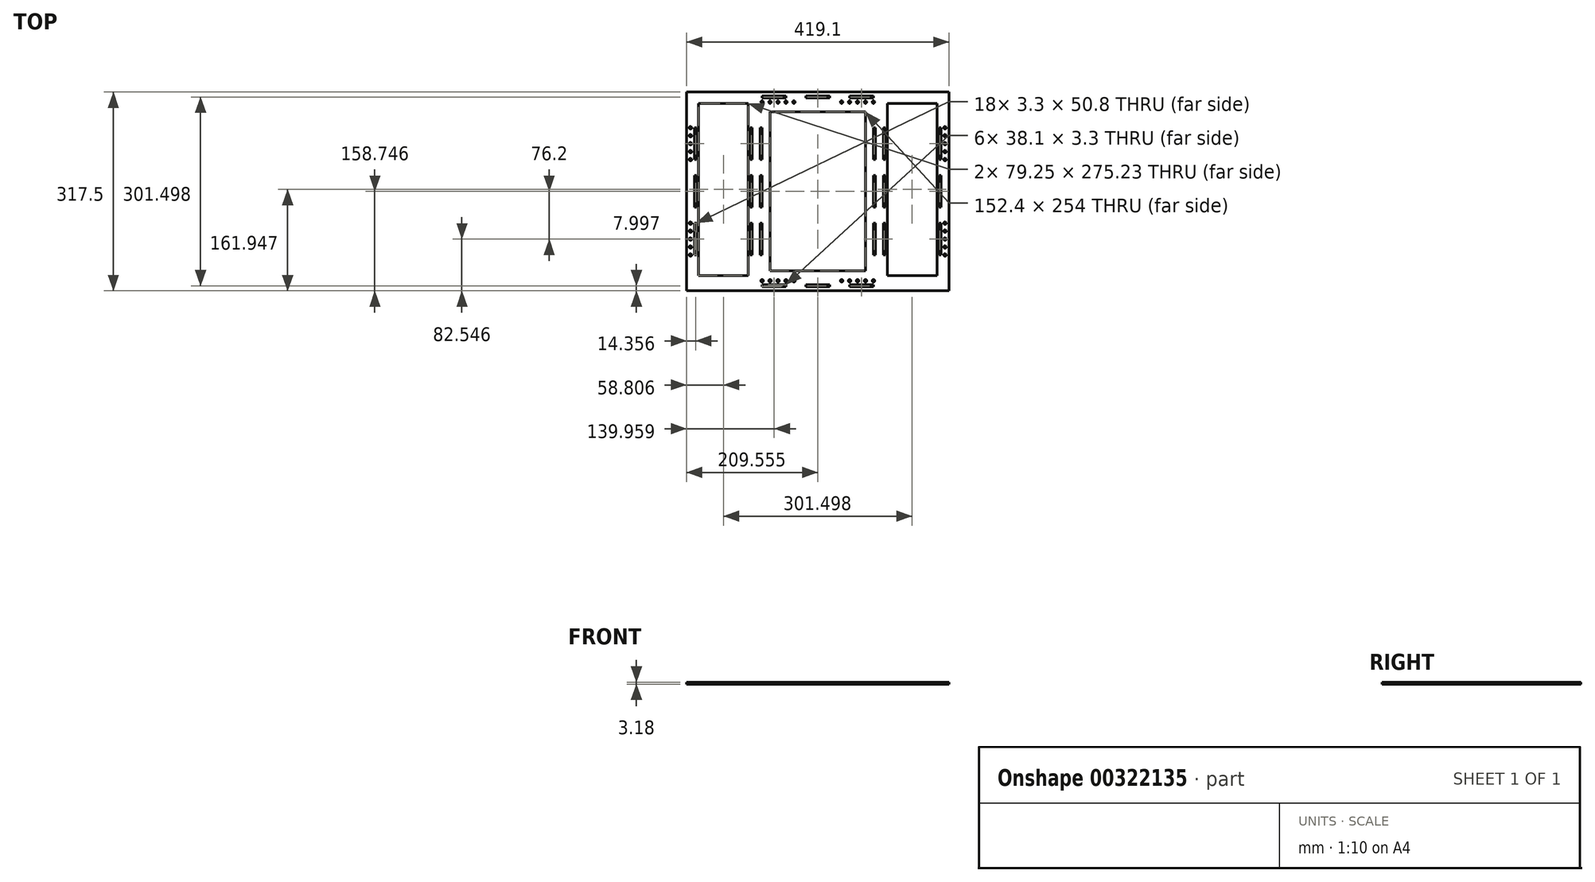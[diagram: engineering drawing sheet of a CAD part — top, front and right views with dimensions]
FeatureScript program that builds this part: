
annotation { "Feature Type Name" : "Feature", "Feature Type Description" : "" }
export const myFeature = defineFeature(function(context is Context, id is Id, definition is map)
    precondition{}
    {
        {
            var Q0;
            Q0=qCreatedBy(makeId("Top.planeOp"),FACE);
            var sketch = newSketch(context, id + "F0", { "sketchPlane" : qUnion([Q0])});
            skCircle(sketch, "E0", {"center": v(-72.78, -151.2) * mm, "radius": 1.98 * mm});
            skCircle(sketch, "E1", {"center": v(-60.08, -151.2) * mm, "radius": 1.98 * mm});
            skCircle(sketch, "E2", {"center": v(-47.38, -151.2) * mm, "radius": 1.98 * mm});
            skCircle(sketch, "E3", {"center": v(-34.68, -151.2) * mm, "radius": 1.98 * mm});
            skCircle(sketch, "E4", {"center": v(-85.48, -151.2) * mm, "radius": 1.98 * mm});
            skCircle(sketch, "E5", {"center": v(41.52, -151.2) * mm, "radius": 1.98 * mm});
            skCircle(sketch, "E6", {"center": v(54.22, -151.2) * mm, "radius": 1.98 * mm});
            skCircle(sketch, "E7", {"center": v(66.92, -151.2) * mm, "radius": 1.98 * mm});
            skCircle(sketch, "E8", {"center": v(79.62, -151.2) * mm, "radius": 1.98 * mm});
            skCircle(sketch, "E9", {"center": v(92.32, -151.2) * mm, "radius": 1.98 * mm});
            skCircle(sketch, "E10.MirrorC", {"center": v(-47.38, 134.3) * mm, "radius": 1.98 * mm});
            skCircle(sketch, "E11.MirrorC", {"center": v(-60.08, 134.3) * mm, "radius": 1.98 * mm});
            skCircle(sketch, "E12.MirrorC", {"center": v(92.32, 134.3) * mm, "radius": 1.98 * mm});
            skCircle(sketch, "E13.MirrorC", {"center": v(-34.68, 134.3) * mm, "radius": 1.98 * mm});
            skCircle(sketch, "E14.MirrorC", {"center": v(-72.78, 134.3) * mm, "radius": 1.98 * mm});
            skCircle(sketch, "E15.MirrorC", {"center": v(-85.48, 134.3) * mm, "radius": 1.98 * mm});
            skCircle(sketch, "E16.MirrorC", {"center": v(54.22, 134.3) * mm, "radius": 1.98 * mm});
            skCircle(sketch, "E17.MirrorC", {"center": v(79.62, 134.3) * mm, "radius": 1.98 * mm});
            skCircle(sketch, "E18.MirrorC", {"center": v(41.52, 134.3) * mm, "radius": 1.98 * mm});
            skCircle(sketch, "E19.MirrorC", {"center": v(66.92, 134.3) * mm, "radius": 1.98 * mm});
            skLineSegment(sketch, "E20.1.0.1", {"start": v(-193.43, 93.16) * mm, "end": v(-193.43, 42.36) * mm});
            skLineSegment(sketch, "E20.1.0.2", {"start": v(-193.43, -59.24) * mm, "end": v(-193.43, -110.04) * mm});
            skLineSegment(sketch, "E20.1.0.4", {"start": v(-193.43, 42.36) * mm, "end": v(-193.43, -33.84) * mm, "construction": true});
            skLineSegment(sketch, "E20.1.0.6", {"start": v(-190.12, -59.24) * mm, "end": v(-190.12, -110.04) * mm});
            skLineSegment(sketch, "E20.1.0.7", {"start": v(-190.12, 16.96) * mm, "end": v(-190.12, -33.84) * mm});
            skLineSegment(sketch, "E20.1.0.9", {"start": v(-186.95, 132.37) * mm, "end": v(-186.95, -142.86) * mm});
            skLineSegment(sketch, "E20.1.0.11", {"start": v(-190.12, 93.16) * mm, "end": v(-190.12, 42.36) * mm});
            skLineSegment(sketch, "E20.1.0.12", {"start": v(-193.43, 16.96) * mm, "end": v(-193.43, -33.84) * mm});
            skLineSegment(sketch, "E20.1.0.14", {"start": v(-193.43, 93.16) * mm, "end": v(-190.12, 93.16) * mm});
            skLineSegment(sketch, "E20.1.0.15", {"start": v(-193.43, -59.24) * mm, "end": v(-190.12, -59.24) * mm});
            skLineSegment(sketch, "E20.1.0.16", {"start": v(-193.43, -110.04) * mm, "end": v(-190.12, -110.04) * mm});
            skLineSegment(sketch, "E20.1.0.17", {"start": v(-193.43, 16.96) * mm, "end": v(-190.12, 16.96) * mm});
            skLineSegment(sketch, "E20.1.0.18", {"start": v(-193.43, 42.36) * mm, "end": v(-190.12, 42.36) * mm});
            skLineSegment(sketch, "E20.1.0.19", {"start": v(-193.43, -33.84) * mm, "end": v(-190.12, -33.84) * mm});
            skLineSegment(sketch, "E21", {"start": v(-206.13, 150.3) * mm, "end": v(-206.13, -167.2) * mm});
            skLineSegment(sketch, "E22.MirrorCS", {"start": v(200.27, -33.84) * mm, "end": v(196.97, -33.84) * mm});
            skLineSegment(sketch, "E23.MirrorCS", {"start": v(200.27, 42.36) * mm, "end": v(196.97, 42.36) * mm});
            skLineSegment(sketch, "E24.MirrorCS", {"start": v(200.27, 93.16) * mm, "end": v(196.97, 93.16) * mm});
            skLineSegment(sketch, "E25.MirrorCS", {"start": v(200.27, -110.04) * mm, "end": v(196.97, -110.04) * mm});
            skLineSegment(sketch, "E26.MirrorCS", {"start": v(200.27, 16.96) * mm, "end": v(196.97, 16.96) * mm});
            skLineSegment(sketch, "E27.MirrorCS", {"start": v(200.27, -59.24) * mm, "end": v(196.97, -59.24) * mm});
            skLineSegment(sketch, "E28.MirrorCS", {"start": v(200.27, 16.96) * mm, "end": v(200.27, -33.84) * mm});
            skLineSegment(sketch, "E29.MirrorCS", {"start": v(200.27, -59.24) * mm, "end": v(200.27, -110.04) * mm});
            skLineSegment(sketch, "E30.MirrorCS", {"start": v(193.8, 132.37) * mm, "end": v(193.8, -142.86) * mm});
            skLineSegment(sketch, "E31.MirrorCS", {"start": v(196.97, -59.24) * mm, "end": v(196.97, -110.04) * mm});
            skLineSegment(sketch, "E32.MirrorCS", {"start": v(200.27, 42.36) * mm, "end": v(200.27, -33.84) * mm, "construction": true});
            skLineSegment(sketch, "E33.MirrorCS", {"start": v(200.27, 93.16) * mm, "end": v(200.27, 42.36) * mm});
            skLineSegment(sketch, "E34.MirrorCS", {"start": v(196.97, 16.96) * mm, "end": v(196.97, -33.84) * mm});
            skLineSegment(sketch, "E35.MirrorCS", {"start": v(196.97, 93.16) * mm, "end": v(196.97, 42.36) * mm});
            skLineSegment(sketch, "E36.MirrorCS", {"start": v(212.97, 150.3) * mm, "end": v(212.97, -167.2) * mm});
            skCircle(sketch, "E37.MirrorC", {"center": v(-199.78, 93.16) * mm, "radius": 1.98 * mm});
            skCircle(sketch, "E38.MirrorC", {"center": v(-199.78, -71.94) * mm, "radius": 1.98 * mm});
            skCircle(sketch, "E39.MirrorC", {"center": v(-199.78, 67.76) * mm, "radius": 1.98 * mm});
            skCircle(sketch, "E40.MirrorC", {"center": v(-199.78, -84.64) * mm, "radius": 1.98 * mm});
            skCircle(sketch, "E41.MirrorC", {"center": v(-199.78, -110.04) * mm, "radius": 1.98 * mm});
            skCircle(sketch, "E42.MirrorC", {"center": v(-199.78, 80.46) * mm, "radius": 1.98 * mm});
            skCircle(sketch, "E43.MirrorC", {"center": v(-199.78, 42.36) * mm, "radius": 1.98 * mm});
            skLineSegment(sketch, "E44.MirrorCS", {"start": v(-193.43, 67.76) * mm, "end": v(-206.13, 67.76) * mm, "construction": true});
            skCircle(sketch, "E45.MirrorC", {"center": v(-199.78, -59.24) * mm, "radius": 1.98 * mm});
            skCircle(sketch, "E46.MirrorC", {"center": v(-199.78, -97.34) * mm, "radius": 1.98 * mm});
            skCircle(sketch, "E47.MirrorC", {"center": v(-199.78, 55.06) * mm, "radius": 1.98 * mm});
            skLineSegment(sketch, "E48.MirrorCS", {"start": v(-190.12, 42.36) * mm, "end": v(-206.13, 42.36) * mm, "construction": true});
            skLineSegment(sketch, "E49.MirrorCS", {"start": v(-193.43, -84.64) * mm, "end": v(-206.13, -84.64) * mm, "construction": true});
            skLineSegment(sketch, "E50.MirrorCS", {"start": v(-199.78, -84.64) * mm, "end": v(-199.78, -110.04) * mm, "construction": true});
            skLineSegment(sketch, "E51.MirrorCS", {"start": v(-199.78, 67.76) * mm, "end": v(-199.78, 93.16) * mm, "construction": true});
            skCircle(sketch, "E52.MirrorC", {"center": v(206.62, -84.64) * mm, "radius": 1.98 * mm});
            skCircle(sketch, "E53.MirrorC", {"center": v(206.62, -71.94) * mm, "radius": 1.98 * mm});
            skCircle(sketch, "E54.MirrorC", {"center": v(206.62, 93.16) * mm, "radius": 1.98 * mm});
            skCircle(sketch, "E55.MirrorC", {"center": v(206.62, 67.76) * mm, "radius": 1.98 * mm});
            skCircle(sketch, "E56.MirrorC", {"center": v(206.62, -110.04) * mm, "radius": 1.98 * mm});
            skCircle(sketch, "E57.MirrorC", {"center": v(206.62, 80.46) * mm, "radius": 1.98 * mm});
            skCircle(sketch, "E58.MirrorC", {"center": v(206.62, 55.06) * mm, "radius": 1.98 * mm});
            skCircle(sketch, "E59.MirrorC", {"center": v(206.62, 42.36) * mm, "radius": 1.98 * mm});
            skCircle(sketch, "E60.MirrorC", {"center": v(206.62, -97.34) * mm, "radius": 1.98 * mm});
            skCircle(sketch, "E61.MirrorC", {"center": v(206.62, -59.24) * mm, "radius": 1.98 * mm});
            skLineSegment(sketch, "E62.MirrorCS", {"start": v(206.62, -84.64) * mm, "end": v(206.62, -110.04) * mm, "construction": true});
            skLineSegment(sketch, "E63.MirrorCS", {"start": v(206.62, 67.76) * mm, "end": v(206.62, 93.16) * mm, "construction": true});
            skLineSegment(sketch, "E64.bottom", {"start": v(114.55, -167.2) * mm, "end": v(-107.7, -167.2) * mm});
            skLineSegment(sketch, "E64.top", {"start": v(114.55, 150.3) * mm, "end": v(-107.7, 150.3) * mm});
            skLineSegment(sketch, "E64.left", {"start": v(114.55, -167.2) * mm, "end": v(114.55, 150.3) * mm, "construction": true});
            skPoint(sketch, "E64.middle", {"position": v(3.42, -8.44) * mm});
            skLineSegment(sketch, "E65.bottom", {"start": v(-85.22, 143.96) * mm, "end": v(-47.12, 143.96) * mm});
            skLineSegment(sketch, "E65.top", {"start": v(-85.22, 140.65) * mm, "end": v(-47.12, 140.65) * mm});
            skLineSegment(sketch, "E65.left", {"start": v(-85.22, 143.96) * mm, "end": v(-85.22, 140.65) * mm});
            skLineSegment(sketch, "E65.right", {"start": v(-47.12, 143.96) * mm, "end": v(-47.12, 140.65) * mm});
            skLineSegment(sketch, "E66.bottom", {"start": v(-15.63, 143.96) * mm, "end": v(22.47, 143.96) * mm});
            skLineSegment(sketch, "E66.top", {"start": v(-15.63, 140.65) * mm, "end": v(22.47, 140.65) * mm});
            skLineSegment(sketch, "E66.left", {"start": v(-15.63, 143.96) * mm, "end": v(-15.63, 140.65) * mm});
            skLineSegment(sketch, "E66.right", {"start": v(22.47, 143.96) * mm, "end": v(22.47, 140.65) * mm});
            skLineSegment(sketch, "E67", {"start": v(-47.12, 143.96) * mm, "end": v(-15.63, 143.96) * mm, "construction": true});
            skLineSegment(sketch, "E68.MirrorCS", {"start": v(92.07, 140.65) * mm, "end": v(53.97, 140.65) * mm});
            skLineSegment(sketch, "E69.MirrorCS", {"start": v(92.07, 143.96) * mm, "end": v(53.97, 143.96) * mm});
            skLineSegment(sketch, "E70.MirrorCS", {"start": v(53.97, 143.96) * mm, "end": v(53.97, 140.65) * mm});
            skLineSegment(sketch, "E71.MirrorCS", {"start": v(92.07, 143.96) * mm, "end": v(92.07, 140.65) * mm});
            skLineSegment(sketch, "E72.MirrorCS", {"start": v(-47.12, -160.84) * mm, "end": v(-47.12, -157.54) * mm});
            skLineSegment(sketch, "E73.MirrorCS", {"start": v(-15.63, -157.54) * mm, "end": v(22.47, -157.54) * mm});
            skLineSegment(sketch, "E74.MirrorCS", {"start": v(22.47, -160.84) * mm, "end": v(22.47, -157.54) * mm});
            skLineSegment(sketch, "E75.MirrorCS", {"start": v(92.07, -157.54) * mm, "end": v(53.97, -157.54) * mm});
            skLineSegment(sketch, "E76.MirrorCS", {"start": v(53.97, -160.84) * mm, "end": v(53.97, -157.54) * mm});
            skLineSegment(sketch, "E77.MirrorCS", {"start": v(-85.22, -157.54) * mm, "end": v(-47.12, -157.54) * mm});
            skLineSegment(sketch, "E78.MirrorCS", {"start": v(92.07, -160.84) * mm, "end": v(92.07, -157.54) * mm});
            skLineSegment(sketch, "E79.MirrorCS", {"start": v(-15.63, -160.84) * mm, "end": v(-15.63, -157.54) * mm});
            skLineSegment(sketch, "E80.MirrorCS", {"start": v(92.07, -160.84) * mm, "end": v(53.97, -160.84) * mm});
            skLineSegment(sketch, "E81.MirrorCS", {"start": v(-15.63, -160.84) * mm, "end": v(22.47, -160.84) * mm});
            skLineSegment(sketch, "E82.MirrorCS", {"start": v(-47.12, -160.84) * mm, "end": v(-15.63, -160.84) * mm, "construction": true});
            skLineSegment(sketch, "E83.MirrorCS", {"start": v(-85.22, -160.84) * mm, "end": v(-47.12, -160.84) * mm});
            skLineSegment(sketch, "E84.MirrorCS", {"start": v(-85.22, -160.84) * mm, "end": v(-85.22, -157.54) * mm});
            skLineSegment(sketch, "E85.bottom", {"start": v(-104.53, 93.16) * mm, "end": v(-101.22, 93.16) * mm});
            skLineSegment(sketch, "E85.top", {"start": v(-104.53, 42.36) * mm, "end": v(-101.22, 42.36) * mm});
            skLineSegment(sketch, "E85.left", {"start": v(-104.53, 93.16) * mm, "end": v(-104.53, 42.36) * mm});
            skLineSegment(sketch, "E85.right", {"start": v(-101.22, 93.16) * mm, "end": v(-101.22, 42.36) * mm});
            skLineSegment(sketch, "E86.0.1.0", {"start": v(-101.22, 16.96) * mm, "end": v(-101.22, -33.84) * mm});
            skLineSegment(sketch, "E86.0.1.1", {"start": v(-104.53, 16.96) * mm, "end": v(-104.53, -33.84) * mm});
            skLineSegment(sketch, "E86.0.1.2", {"start": v(-104.53, 16.96) * mm, "end": v(-101.22, 16.96) * mm});
            skLineSegment(sketch, "E86.0.1.3", {"start": v(-104.53, -33.84) * mm, "end": v(-101.22, -33.84) * mm});
            skLineSegment(sketch, "E86.0.2.0", {"start": v(-101.22, -59.24) * mm, "end": v(-101.22, -110.04) * mm});
            skLineSegment(sketch, "E86.0.2.1", {"start": v(-104.53, -59.24) * mm, "end": v(-104.53, -110.04) * mm});
            skLineSegment(sketch, "E86.0.2.2", {"start": v(-104.53, -59.24) * mm, "end": v(-101.22, -59.24) * mm});
            skLineSegment(sketch, "E86.0.2.3", {"start": v(-104.53, -110.04) * mm, "end": v(-101.22, -110.04) * mm});
            skLineSegment(sketch, "E86.direction1", {"start": v(-104.53, 42.36) * mm, "end": v(-88.52, 42.36) * mm, "construction": true});
            skLineSegment(sketch, "E86.direction2", {"start": v(-104.53, 42.36) * mm, "end": v(-104.53, -33.84) * mm, "construction": true});
            skLineSegment(sketch, "E87.MirrorCS", {"start": v(108.07, 16.96) * mm, "end": v(108.07, -33.84) * mm});
            skLineSegment(sketch, "E88.MirrorCS", {"start": v(111.37, -59.24) * mm, "end": v(108.07, -59.24) * mm});
            skLineSegment(sketch, "E89.MirrorCS", {"start": v(111.37, 16.96) * mm, "end": v(111.37, -33.84) * mm});
            skLineSegment(sketch, "E90.MirrorCS", {"start": v(111.37, -110.04) * mm, "end": v(108.07, -110.04) * mm});
            skLineSegment(sketch, "E91.MirrorCS", {"start": v(111.37, 16.96) * mm, "end": v(108.07, 16.96) * mm});
            skLineSegment(sketch, "E92.MirrorCS", {"start": v(111.37, -33.84) * mm, "end": v(108.07, -33.84) * mm});
            skLineSegment(sketch, "E93.MirrorCS", {"start": v(111.37, 42.36) * mm, "end": v(111.37, -33.84) * mm, "construction": true});
            skLineSegment(sketch, "E94.MirrorCS", {"start": v(111.37, 93.16) * mm, "end": v(108.07, 93.16) * mm});
            skLineSegment(sketch, "E95.MirrorCS", {"start": v(111.37, 42.36) * mm, "end": v(108.07, 42.36) * mm});
            skLineSegment(sketch, "E96.MirrorCS", {"start": v(111.37, 93.16) * mm, "end": v(111.37, 42.36) * mm});
            skLineSegment(sketch, "E97.MirrorCS", {"start": v(108.07, -59.24) * mm, "end": v(108.07, -110.04) * mm});
            skLineSegment(sketch, "E98.MirrorCS", {"start": v(108.07, 93.16) * mm, "end": v(108.07, 42.36) * mm});
            skLineSegment(sketch, "E99.MirrorCS", {"start": v(111.37, -59.24) * mm, "end": v(111.37, -110.04) * mm});
            skLineSegment(sketch, "E100.0.1.0", {"start": v(-85.22, 93.16) * mm, "end": v(-85.22, 42.36) * mm});
            skLineSegment(sketch, "E100.3.1.0", {"start": v(-88.52, 93.16) * mm, "end": v(-88.52, 42.36) * mm});
            skLineSegment(sketch, "E100.6.1.0", {"start": v(-88.52, 93.16) * mm, "end": v(-85.22, 93.16) * mm});
            skLineSegment(sketch, "E100.9.1.0", {"start": v(-88.52, 42.36) * mm, "end": v(-85.22, 42.36) * mm});
            skLineSegment(sketch, "E100.0.1.1", {"start": v(-85.22, 16.96) * mm, "end": v(-85.22, -33.84) * mm});
            skLineSegment(sketch, "E100.3.1.1", {"start": v(-88.52, 16.96) * mm, "end": v(-88.52, -33.84) * mm});
            skLineSegment(sketch, "E100.6.1.1", {"start": v(-88.52, 16.96) * mm, "end": v(-85.22, 16.96) * mm});
            skLineSegment(sketch, "E100.9.1.1", {"start": v(-88.52, -33.84) * mm, "end": v(-85.22, -33.84) * mm});
            skLineSegment(sketch, "E100.0.1.2", {"start": v(-85.22, -59.24) * mm, "end": v(-85.22, -110.04) * mm});
            skLineSegment(sketch, "E100.3.1.2", {"start": v(-88.52, -59.24) * mm, "end": v(-88.52, -110.04) * mm});
            skLineSegment(sketch, "E100.6.1.2", {"start": v(-88.52, -59.24) * mm, "end": v(-85.22, -59.24) * mm});
            skLineSegment(sketch, "E100.9.1.2", {"start": v(-88.52, -110.04) * mm, "end": v(-85.22, -110.04) * mm});
            skLineSegment(sketch, "E101.MirrorCS", {"start": v(95.37, 93.16) * mm, "end": v(95.37, 42.36) * mm});
            skLineSegment(sketch, "E102.MirrorCS", {"start": v(95.37, 93.16) * mm, "end": v(92.07, 93.16) * mm});
            skLineSegment(sketch, "E103.MirrorCS", {"start": v(95.37, 42.36) * mm, "end": v(92.07, 42.36) * mm});
            skLineSegment(sketch, "E104.MirrorCS", {"start": v(95.37, -59.24) * mm, "end": v(95.37, -110.04) * mm});
            skLineSegment(sketch, "E105.MirrorCS", {"start": v(92.07, 16.96) * mm, "end": v(92.07, -33.84) * mm});
            skLineSegment(sketch, "E106.MirrorCS", {"start": v(95.37, -59.24) * mm, "end": v(92.07, -59.24) * mm});
            skLineSegment(sketch, "E107.MirrorCS", {"start": v(95.37, 16.96) * mm, "end": v(95.37, -33.84) * mm});
            skLineSegment(sketch, "E108.MirrorCS", {"start": v(95.37, -110.04) * mm, "end": v(92.07, -110.04) * mm});
            skLineSegment(sketch, "E109.MirrorCS", {"start": v(95.37, 16.96) * mm, "end": v(92.07, 16.96) * mm});
            skLineSegment(sketch, "E110.MirrorCS", {"start": v(95.37, -33.84) * mm, "end": v(92.07, -33.84) * mm});
            skLineSegment(sketch, "E111.MirrorCS", {"start": v(92.07, 93.16) * mm, "end": v(92.07, 42.36) * mm});
            skLineSegment(sketch, "E112.MirrorCS", {"start": v(92.07, -59.24) * mm, "end": v(92.07, -110.04) * mm});
            skLineSegment(sketch, "E113", {"start": v(-85.22, 93.16) * mm, "end": v(-85.22, 140.65) * mm, "construction": true});
            skLineSegment(sketch, "E114", {"start": v(114.55, 150.3) * mm, "end": v(212.97, 150.3) * mm});
            skLineSegment(sketch, "E115", {"start": v(212.97, -167.2) * mm, "end": v(114.55, -167.2) * mm});
            skLineSegment(sketch, "E116.bottom", {"start": v(114.55, 132.37) * mm, "end": v(193.8, 132.37) * mm});
            skLineSegment(sketch, "E116.top", {"start": v(114.55, -142.86) * mm, "end": v(193.8, -142.86) * mm});
            skLineSegment(sketch, "E116.left", {"start": v(114.55, 132.37) * mm, "end": v(114.55, -142.86) * mm});
            skLineSegment(sketch, "E117.MirrorCS", {"start": v(-107.7, -167.2) * mm, "end": v(-107.7, 150.3) * mm, "construction": true});
            skLineSegment(sketch, "E118.MirrorCS", {"start": v(-107.7, 150.3) * mm, "end": v(-206.13, 150.3) * mm});
            skLineSegment(sketch, "E119.MirrorCS", {"start": v(-206.13, -167.2) * mm, "end": v(-107.7, -167.2) * mm});
            skLineSegment(sketch, "E120.MirrorCS", {"start": v(-107.7, -142.86) * mm, "end": v(-186.95, -142.86) * mm});
            skLineSegment(sketch, "E121.MirrorCS", {"start": v(-107.7, 132.37) * mm, "end": v(-186.95, 132.37) * mm});
            skLineSegment(sketch, "E122", {"start": v(-107.7, 132.37) * mm, "end": v(-107.7, -142.86) * mm});
            skPoint(sketch, "E123", {"position": v(3.42, 140.65) * mm});
            skLineSegment(sketch, "E124.bottom", {"start": v(79.62, -135.44) * mm, "end": v(-72.78, -135.44) * mm});
            skLineSegment(sketch, "E124.top", {"start": v(79.62, 118.56) * mm, "end": v(-72.78, 118.56) * mm});
            skLineSegment(sketch, "E124.left", {"start": v(79.62, -135.44) * mm, "end": v(79.62, 118.56) * mm});
            skLineSegment(sketch, "E124.right", {"start": v(-72.78, -135.44) * mm, "end": v(-72.78, 118.56) * mm});
            skSolve(sketch);
        }
        {
            var Q0;
            Q0=makeQuery(id+"F0.imprint","IMPRINT",FACE,{"disambiguationData":[TD([[makeQuery(id+"F0.imprint","IMPRINT",EDGE,{"derivedFrom":sQuery(id+"F0.wireOp",EDGE,"E0")}),-1.0]])]});
            extrude(context, id + "F1", {"entities" : qUnion([Q0]), "depth" : 3.17 * mm});
        }
    });
